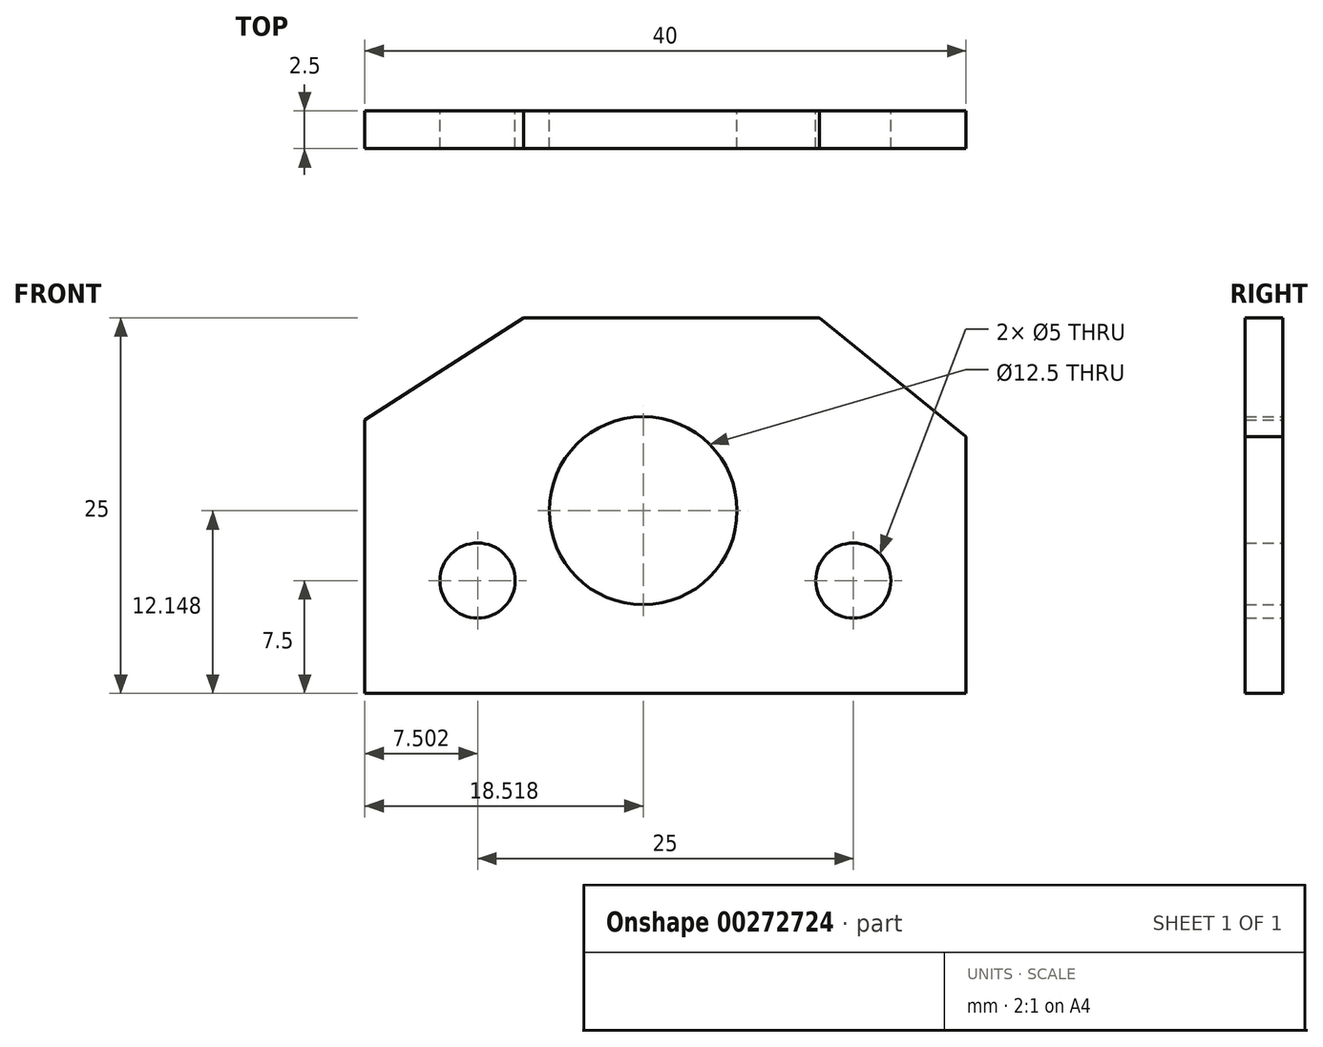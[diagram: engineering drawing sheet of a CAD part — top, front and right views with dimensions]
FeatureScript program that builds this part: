
annotation { "Feature Type Name" : "Feature", "Feature Type Description" : "" }
export const myFeature = defineFeature(function(context is Context, id is Id, definition is map)
    precondition{}
    {
        {
            var Q0;
            Q0=qCreatedBy(makeId("Front.planeOp"),FACE);
            var sketch = newSketch(context, id + "F0", { "sketchPlane" : qUnion([Q0])});
            skLineSegment(sketch, "E0", {"start": v(-24.6, 10.7) * mm, "end": v(-24.6, -7.5) * mm});
            skLineSegment(sketch, "E1", {"start": v(-24.6, -7.5) * mm, "end": v(15.4, -7.5) * mm});
            skLineSegment(sketch, "E2", {"start": v(15.4, -7.5) * mm, "end": v(15.4, 9.6) * mm});
            skLineSegment(sketch, "E3", {"start": v(15.4, 9.6) * mm, "end": v(5.63, 17.5) * mm});
            skLineSegment(sketch, "E4", {"start": v(-24.6, 10.7) * mm, "end": v(-14.03, 17.5) * mm});
            skLineSegment(sketch, "E5", {"start": v(-14.03, 17.5) * mm, "end": v(5.63, 17.5) * mm});
            skCircle(sketch, "E6", {"center": v(-6.08, 4.65) * mm, "radius": 6.25 * mm});
            skCircle(sketch, "E7", {"center": v(-17.1, 0) * mm, "radius": 2.5 * mm});
            skCircle(sketch, "E8", {"center": v(7.9, 0) * mm, "radius": 2.5 * mm});
            skLineSegment(sketch, "E9", {"start": v(-4.6, -7.5) * mm, "end": v(-4.6, 26.87) * mm, "construction": true});
            skSolve(sketch);
        }
        {
            var Q0;
            Q0=makeQuery(id+"F0.imprint","IMPRINT",FACE,{"disambiguationData":[TD([[makeQuery(id+"F0.imprint","IMPRINT",EDGE,{"derivedFrom":sQuery(id+"F0.wireOp",EDGE,"E0")}),1.0]])]});
            extrude(context, id + "F1", {"entities" : qUnion([Q0]), "depth" : 2.5 * mm});
        }
    });
